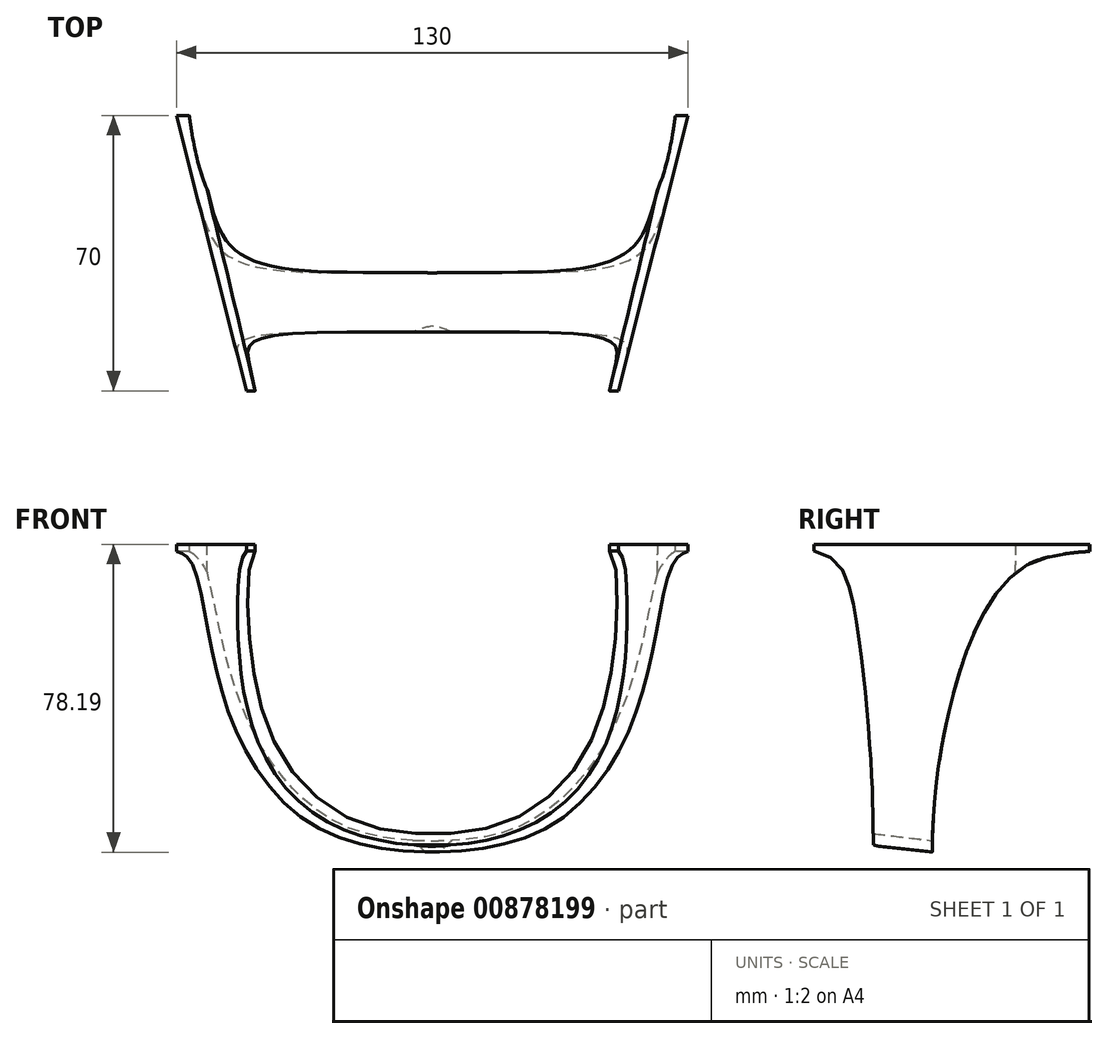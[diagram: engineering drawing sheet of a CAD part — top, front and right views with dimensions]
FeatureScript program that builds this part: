
annotation { "Feature Type Name" : "Feature", "Feature Type Description" : "" }
export const myFeature = defineFeature(function(context is Context, id is Id, definition is map)
    precondition{}
    {
        {
            var Q0;
            Q0=qCreatedBy(makeId("Right.planeOp"),FACE);
            var sketch = newSketch(context, id + "F0", { "sketchPlane" : qUnion([Q0])});
            skLineSegment(sketch, "E0.bottom", {"start": v(-35, 40) * mm, "end": v(35, 40) * mm});
            skLineSegment(sketch, "E0.left", {"start": v(-35, 40) * mm, "end": v(-35, 38.39) * mm});
            skLineSegment(sketch, "E0.right", {"start": v(35, 40) * mm, "end": v(35, 38.22) * mm});
            skLineSegment(sketch, "E1", {"start": v(-5, 70.93) * mm, "end": v(-5, -98.54) * mm, "construction": true});
            skLineSegment(sketch, "E2", {"start": v(-20, 70.77) * mm, "end": v(-20, -98.6) * mm, "construction": true});
            skFitSpline(sketch, "E3", {"points": [v(-39.42, 39.01) * mm, v(-25.48, 26.71) * mm, v(-21.22, -6.69) * mm, v(-20, -36.36) * mm], "startDerivative": vector(112.65, -7.04) * mm, "endDerivative": vector(0, -105.28) * mm});
            skFitSpline(sketch, "E4", {"points": [v(46.26, 38.56) * mm, v(15.08, 31.9) * mm, v(3.53, 12.27) * mm, v(-3.44, -16.6) * mm, v(-5, -40) * mm], "startDerivative": vector(-207.3, -1.92) * mm, "endDerivative": vector(0, -119.8) * mm});
            skLineSegment(sketch, "E5", {"start": v(-5, -40) * mm, "end": v(-20, -36.36) * mm});
            skSolve(sketch);
        }
        {
            var Q0;
            Q0=makeQuery(id+"F0.imprint","IMPRINT",FACE,{"disambiguationData":[TD([[makeQuery(id+"F0.imprint","IMPRINT",EDGE,{"derivedFrom":sQuery(id+"F0.wireOp",EDGE,"E0.bottom")}),-1.0]])]});
            extrude(context, id + "F1", {"entities" : qUnion([Q0]), "endBound" : BoundingType.SYMMETRIC, "depth" : 130 * mm, "offsetDistance" : 25 * mm});
        }
        {
            var Q0;
            Q0=qCreatedBy(makeId("Top.planeOp"),FACE);
            var sketch = newSketch(context, id + "F2", { "sketchPlane" : qUnion([Q0])});
            skLineSegment(sketch, "E6", {"start": v(0, -52.78) * mm, "end": v(0, 83.46) * mm, "construction": true});
            skLineSegment(sketch, "E7", {"start": v(81.22, -35) * mm, "end": v(-96.86, -35) * mm, "construction": true});
            skLineSegment(sketch, "E8", {"start": v(83.8, -5) * mm, "end": v(-100.38, -5) * mm, "construction": true});
            skLineSegment(sketch, "E9", {"start": v(77.26, -20) * mm, "end": v(-87.56, -20) * mm, "construction": true});
            skLineSegment(sketch, "E10", {"start": v(65, -51.77) * mm, "end": v(65, 72.54) * mm, "construction": true});
            skLineSegment(sketch, "E11", {"start": v(-65, -49.2) * mm, "end": v(-65, 59.54) * mm, "construction": true});
            skFitSpline(sketch, "E12", {"points": [v(0, -5) * mm, v(44.7, 2.45) * mm, v(58.35, 19.08) * mm, v(62.58, 43.3) * mm, v(63.13, 54.8) * mm], "startDerivative": vector(186.2, 0) * mm, "endDerivative": vector(5.37, 147.65) * mm});
            skLineSegment(sketch, "E13", {"start": v(63.13, 54.8) * mm, "end": v(0, 54.8) * mm});
            skLineSegment(sketch, "E14.MirrorCS", {"start": v(-63.13, 54.8) * mm, "end": v(0, 54.8) * mm});
            skFitSpline(sketch, "E15.MirrorCS", {"points": [v(0, -5) * mm, v(-44.7, 2.45) * mm, v(-58.35, 19.08) * mm, v(-62.58, 43.3) * mm, v(-63.13, 54.8) * mm], "startDerivative": vector(-186.2, 0) * mm, "endDerivative": vector(-5.37, 147.65) * mm});
            skLineSegment(sketch, "E16", {"start": v(-45, 80.3) * mm, "end": v(-45, -91.1) * mm, "construction": true});
            skFitSpline(sketch, "E17", {"points": [v(0, -20) * mm, v(-16.21, -21.5) * mm, v(-27.25, -24.63) * mm, v(-36.47, -29.35) * mm, v(-44.3, -44.56) * mm], "startDerivative": vector(-73.88, -0.77) * mm, "endDerivative": vector(-3.32, -97.99) * mm});
            skFitSpline(sketch, "E18.MirrorCS", {"points": [v(0, -20) * mm, v(16.21, -21.5) * mm, v(27.25, -24.63) * mm, v(36.47, -29.35) * mm, v(44.3, -44.56) * mm], "startDerivative": vector(73.88, -0.77) * mm, "endDerivative": vector(3.32, -97.99) * mm});
            skSolve(sketch);
        }
        {
            var Q0;
            Q0=makeQuery(id+"F2.imprint","IMPRINT",FACE,{"disambiguationData":[TD([[makeQuery(id+"F2.imprint","IMPRINT",EDGE,{"derivedFrom":sQuery(id+"F2.wireOp",EDGE,"E12")}),1.0]])]});
            var Q1;
            Q1=makeQuery(id+"F2.imprint","IMPRINT",FACE,{"disambiguationData":[TD([[makeQuery(id+"F2.imprint","IMPRINT",EDGE,{"derivedFrom":sQuery(id+"F2.wireOp",EDGE,"625081aa-0078-453e-aa18-fec9ced59822")}),-1.0]])]});
            extrude(context, id + "F3", {"entities" : qUnion([Q0, Q1]), "operationType" : NewBodyOperationType.REMOVE, "endBound" : BoundingType.THROUGH_ALL, "oppositeDirection" : true, "depth" : 25 * mm, "offsetDistance" : 25 * mm, "hasSecondDirection" : true, "secondDirectionOppositeDirection" : false, "secondDirectionDepth" : 85.9 * mm});
        }
        {
            var Q0;
            {var subQ0=sQuery(id+"F0.wireOp",EDGE,"E0.bottom");var subQ1=sQuery(id+"F0.wireOp",EDGE,"E0.left");Q0=makeQuery(id+"F3.boolean.opBoolean","SPLIT",EDGE,{"disambiguationData":[TD([makeQuery(id+"F3.opExtrude","SWEPT_FACE",FACE,{"disambiguationData":[OSD([sQuery(id+"F2.wireOp",EDGE,"f082029b-4e69-4655-94c5-f63c338ab6170.MirrorCS")])]})])],"derivedFrom":makeQuery(id+"F1.opExtrude","SWEPT_EDGE",EDGE,{"disambiguationData":[OSD([subQ0,subQ1])]})});}
            cPoint(context, id + "F4", {"entities" : qUnion([Q0]), "parameter" : 0.5});
        }
        {
            var Q0;
            Q0 = qCreatedBy(id + "F4" ,VERTEX);
            var Q1;
            {var subQ2=sQuery(id+"F0.wireOp",EDGE,"E0.left");Q1=makeQuery(id+"F3.boolean.opBoolean","SPLIT",FACE,{"disambiguationData":[TD([makeQuery(id+"F3.opExtrude","SWEPT_FACE",FACE,{"disambiguationData":[OSD([sQuery(id+"F2.wireOp",EDGE,"f082029b-4e69-4655-94c5-f63c338ab6170.MirrorCS")])]})])],"derivedFrom":makeQuery(id+"F1.opExtrude","SWEPT_FACE",FACE,{"disambiguationData":[OSD([subQ2])]})});}
            cPlane(context, id + "F5", {"entities" : qUnion([Q0, Q1]), "cplaneType" : CPlaneType.PLANE_POINT, "offset" : 25 * mm, "width" : 150 * mm, "height" : 150 * mm});
        }
        {
            var Q0;
            {var subQ2=sQuery(id+"F0.wireOp",EDGE,"E0.right");Q0=makeQuery(id+"F3.boolean.opBoolean","SPLIT",FACE,{"disambiguationData":[TD([makeQuery(id+"F3.opExtrude","SWEPT_FACE",FACE,{"disambiguationData":[OSD([sQuery(id+"F2.wireOp",EDGE,"E15.MirrorCS")])]})])],"derivedFrom":makeQuery(id+"F1.opExtrude","SWEPT_FACE",FACE,{"disambiguationData":[OSD([subQ2])]})});}
            cPlane(context, id + "F6", {"entities" : qUnion([Q0]), "cplaneType" : CPlaneType.OFFSET, "offset" : 0 * mm, "width" : 150 * mm, "height" : 150 * mm});
        }
        {
            var Q0;
            Q0=qCreatedBy(id+"F5.planeOp",FACE);
            var sketch = newSketch(context, id + "F7", { "sketchPlane" : qUnion([Q0])});
            skLineSegment(sketch, "E19", {"start": v(-390.13, -36.36) * mm, "end": v(107.8, -36.36) * mm, "construction": true});
            skLineSegment(sketch, "E20", {"start": v(-175.24, -40) * mm, "end": v(125.06, -40) * mm, "construction": true});
            skLineSegment(sketch, "E21", {"start": v(-45, 43.96) * mm, "end": v(-45, 18.14) * mm, "construction": true});
            skLineSegment(sketch, "E22", {"start": v(-45, 40.65) * mm, "end": v(45, 40.65) * mm});
            skFitSpline(sketch, "E23", {"points": [v(-45, 40.65) * mm, v(-37.4, -9.81) * mm, v(-24.6, -24.78) * mm, v(0, -31.72) * mm], "startDerivative": vector(0, -134.53) * mm, "endDerivative": vector(121.81, 1.19) * mm});
            skFitSpline(sketch, "E24.MirrorCS", {"points": [v(45, 40.65) * mm, v(37.4, -9.81) * mm, v(24.6, -24.78) * mm, v(0, -31.72) * mm], "startDerivative": vector(0, -134.53) * mm, "endDerivative": vector(-121.81, 1.19) * mm});
            skLineSegment(sketch, "E25", {"start": v(0, 89.99) * mm, "end": v(0, -96.04) * mm, "construction": true});
            skFitSpline(sketch, "E26", {"points": [v(0, -34.91) * mm, v(25.39, -28.32) * mm, v(40.35, -11.7) * mm, v(47.2, 45.24) * mm], "startDerivative": vector(101.55, 1.14) * mm, "endDerivative": vector(-1.75, 185.58) * mm});
            skFitSpline(sketch, "E27.MirrorCS", {"points": [v(0, -34.91) * mm, v(-25.39, -28.32) * mm, v(-40.35, -11.7) * mm, v(-47.2, 45.24) * mm], "startDerivative": vector(-101.55, 1.14) * mm, "endDerivative": vector(1.75, 185.58) * mm});
            skLineSegment(sketch, "E28", {"start": v(47.2, 45.24) * mm, "end": v(70.92, 45.24) * mm});
            skLineSegment(sketch, "E29", {"start": v(70.92, 45.24) * mm, "end": v(70.92, -46.7) * mm});
            skLineSegment(sketch, "E30", {"start": v(70.92, -46.7) * mm, "end": v(0, -46.7) * mm});
            skLineSegment(sketch, "E31.MirrorCS", {"start": v(-47.2, 45.24) * mm, "end": v(-70.92, 45.24) * mm});
            skLineSegment(sketch, "E32.MirrorCS", {"start": v(-70.92, 45.24) * mm, "end": v(-70.92, -46.7) * mm});
            skLineSegment(sketch, "E33.MirrorCS", {"start": v(-70.92, -46.7) * mm, "end": v(0, -46.7) * mm});
            skSolve(sketch);
        }
        {
            var Q0;
            Q0=qCreatedBy(id+"F6.planeOp",FACE);
            var sketch = newSketch(context, id + "F8", { "sketchPlane" : qUnion([Q0])});
            skLineSegment(sketch, "E34", {"start": v(-65, 49.74) * mm, "end": v(-65, -56.78) * mm, "construction": true});
            skLineSegment(sketch, "E35", {"start": v(-82, -40) * mm, "end": v(72.16, -40) * mm, "construction": true});
            skLineSegment(sketch, "E36", {"start": v(-61.74, 48.88) * mm, "end": v(-61.74, 3.8) * mm, "construction": true});
            skFitSpline(sketch, "E37", {"points": [v(-61.74, 40.74) * mm, v(-57.46, 1.6) * mm, v(-35.5, -30.93) * mm, v(0, -40) * mm], "startDerivative": vector(0, -164.94) * mm, "endDerivative": vector(153.73, 0) * mm});
            skFitSpline(sketch, "E38.MirrorCS", {"points": [v(61.74, 40.74) * mm, v(57.46, 1.6) * mm, v(35.5, -30.93) * mm, v(0, -40) * mm], "startDerivative": vector(0, -164.94) * mm, "endDerivative": vector(-153.73, 0) * mm});
            skLineSegment(sketch, "E39", {"start": v(-61.74, 40.74) * mm, "end": v(61.74, 40.74) * mm});
            skFitSpline(sketch, "E40", {"points": [v(-65, 53.65) * mm, v(-60.73, -1.27) * mm, v(-37.15, -35.04) * mm, v(0, -42.55) * mm], "startDerivative": vector(0, -201.72) * mm, "endDerivative": vector(136.88, -3.24) * mm});
            skFitSpline(sketch, "E41.MirrorCS", {"points": [v(65, 53.65) * mm, v(60.73, -1.27) * mm, v(37.15, -35.04) * mm, v(0, -42.55) * mm], "startDerivative": vector(0, -201.72) * mm, "endDerivative": vector(-136.88, -3.24) * mm});
            skLineSegment(sketch, "E42", {"start": v(-65, 53.65) * mm, "end": v(-87.8, 53.65) * mm});
            skLineSegment(sketch, "E43", {"start": v(-87.8, 53.65) * mm, "end": v(-87.8, -53.51) * mm});
            skLineSegment(sketch, "E44", {"start": v(-87.8, -53.51) * mm, "end": v(0, -53.51) * mm});
            skLineSegment(sketch, "E45.MirrorCS", {"start": v(65, 53.65) * mm, "end": v(87.8, 53.65) * mm});
            skLineSegment(sketch, "E46.MirrorCS", {"start": v(87.8, 53.65) * mm, "end": v(87.8, -53.51) * mm});
            skLineSegment(sketch, "E47.MirrorCS", {"start": v(87.8, -53.51) * mm, "end": v(0, -53.51) * mm});
            skSolve(sketch);
        }
        {
            var Q1;
            Q1=makeQuery(id+"F7.imprint","IMPRINT",FACE,{"disambiguationData":[TD([[makeQuery(id+"F7.imprint","IMPRINT",EDGE,{"derivedFrom":sQuery(id+"F7.wireOp",EDGE,"E22")}),-1.0]])]});
            var Q2;
            Q2=makeQuery(id+"F8.imprint","IMPRINT",FACE,{"disambiguationData":[TD([[makeQuery(id+"F8.imprint","IMPRINT",EDGE,{"derivedFrom":sQuery(id+"F8.wireOp",EDGE,"E37")}),1.0]])]});
            loft(context, id + "F9", {"operationType" : NewBodyOperationType.REMOVE, "sheetProfilesArray" : [{ "sheetProfileEntities" : qUnion([Q1]) }, { "sheetProfileEntities" : qUnion([Q2]) }]});
        }
        {
            var Q1;
            Q1=makeQuery(id+"F7.imprint","IMPRINT",FACE,{"disambiguationData":[TD([[makeQuery(id+"F7.imprint","IMPRINT",EDGE,{"derivedFrom":sQuery(id+"F7.wireOp",EDGE,"E26")}),-1.0]])]});
            var Q2;
            Q2=makeQuery(id+"F8.imprint","IMPRINT",FACE,{"disambiguationData":[TD([[makeQuery(id+"F8.imprint","IMPRINT",EDGE,{"derivedFrom":sQuery(id+"F8.wireOp",EDGE,"E40")}),-1.0]])]});
            loft(context, id + "F10", {"operationType" : NewBodyOperationType.REMOVE, "sheetProfilesArray" : [{ "sheetProfileEntities" : qUnion([Q1]) }, { "sheetProfileEntities" : qUnion([Q2]) }]});
        }
    });
